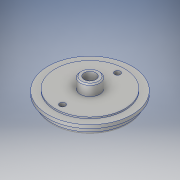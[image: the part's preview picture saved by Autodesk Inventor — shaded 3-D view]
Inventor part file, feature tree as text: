
AUTODESK INVENTOR PART (.ipt)
format: ipt  version: 2017 (Build 210142000, 142)  size: 169,472 bytes
history: native  units: in
note: dims shown in document units (in); Inventor stores cm internally (conversion verified against a paired STEP export)
features: sketch x3, hole x2, chamfer x2, revolve x1, fillet x1
ambient origin geometry x8: Origin, YZ Plane, XZ Plane, XY Plane, X Axis, Y Axis, Z Axis, Center Point
bodies: Solid1 (feature_tree)
feature tree (9):
  revolve  "Revolution1"  [1 undecoded]
  hole  "Hole1"  [1 undecoded]
  fillet  "Fillet1"  Radius=1.4975in
  hole  "Hole2"  [1 undecoded]
  chamfer  "Chamfer1"  Distance=0.125in
  chamfer  "Chamfer2"  Distance=0.47in
  sketch  "Sketch1"  dims[d1=0.5in d3=0.147in d5=0.195in d8=0.691in d9=1.668in]
  sketch  "Sketch2"  dims[d10=1.814in d11=0.062in d12=1.4975in]
  sketch  "Sketch3"  dims[d13=90.0deg d14=2.376in d15=0.25in d16=0.75in d17=0.375in d18=0.25in d19=0.5635in d20=0.3in d21=0.0in d22=0.125in d23=0.47in d24=0.419in d25=0.511in d26=0.5in d27=0.375in d28=0.25in d29=0.5635in d30=2.0in d31=0.8108in d32=0.05in d33=0.125in d34=45.0deg d35=0.05in d36=0.125in d37=45.0deg]
note: 3 required parameter values undecoded (feature->parameter linkage not recoverable at this tier; creation-order binding heuristic only, values carry confidence <= 0.55)